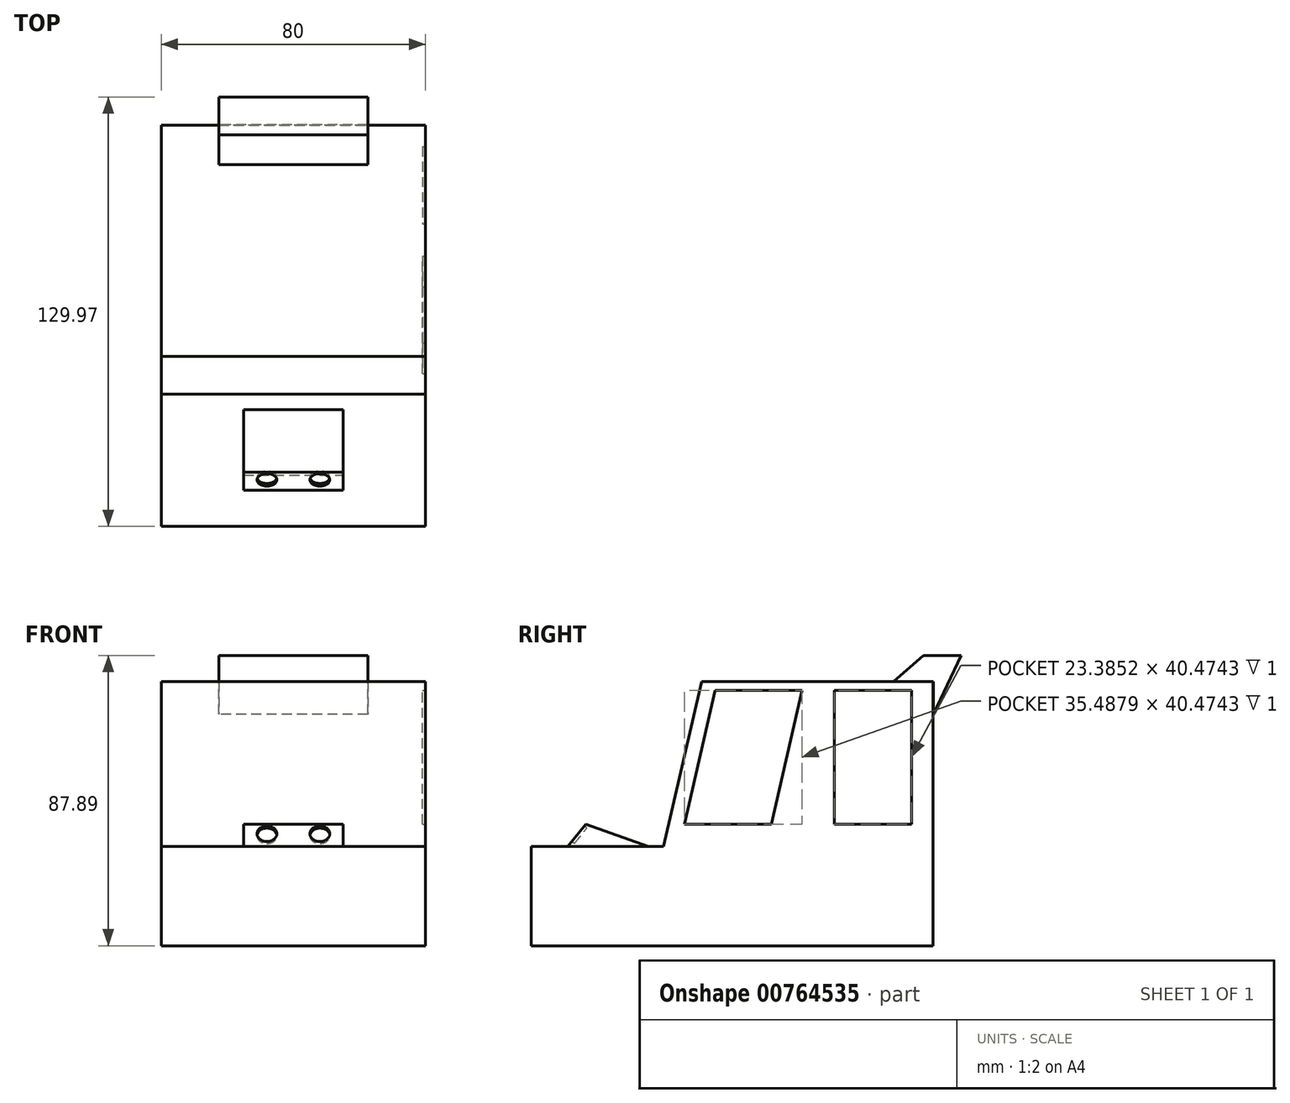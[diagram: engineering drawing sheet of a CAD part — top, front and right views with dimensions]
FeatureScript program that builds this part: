
annotation { "Feature Type Name" : "Feature", "Feature Type Description" : "" }
export const myFeature = defineFeature(function(context is Context, id is Id, definition is map)
    precondition{}
    {
        {
            var Q0;
            Q0=qCreatedBy(makeId("Right.planeOp"),FACE);
            var sketch = newSketch(context, id + "F0", { "sketchPlane" : qUnion([Q0])});
            skLineSegment(sketch, "E0", {"start": v(-34.5, 43.18) * mm, "end": v(35.5, 43.18) * mm});
            skLineSegment(sketch, "E1", {"start": v(35.5, 43.18) * mm, "end": v(35.5, -36.82) * mm});
            skLineSegment(sketch, "E2", {"start": v(35.5, -36.82) * mm, "end": v(-86, -36.82) * mm});
            skLineSegment(sketch, "E3", {"start": v(-86, -36.82) * mm, "end": v(-86, -6.82) * mm});
            skLineSegment(sketch, "E4", {"start": v(-86, -6.82) * mm, "end": v(-46, -6.82) * mm});
            skLineSegment(sketch, "E5", {"start": v(-46, -6.82) * mm, "end": v(-34.5, 43.18) * mm});
            skSolve(sketch);
        }
        {
            var Q0;
            Q0=makeQuery(id+"F0.imprint","IMPRINT",FACE,{"disambiguationData":[TD([[makeQuery(id+"F0.imprint","IMPRINT",EDGE,{"derivedFrom":sQuery(id+"F0.wireOp",EDGE,"E0")}),-1.0]])]});
            extrude(context, id + "F1", {"entities" : qUnion([Q0]), "endBound" : BoundingType.SYMMETRIC, "depth" : 80 * mm, "offsetDistance" : 25 * mm});
        }
        {
            var Q0;
            Q0=qCreatedBy(makeId("Right.planeOp"),FACE);
            var sketch = newSketch(context, id + "F2", { "sketchPlane" : qUnion([Q0])});
            skLineSegment(sketch, "E6", {"start": v(35.58, 33.28) * mm, "end": v(43.97, 51.07) * mm});
            skLineSegment(sketch, "E7", {"start": v(43.97, 51.07) * mm, "end": v(32.58, 51.07) * mm});
            skLineSegment(sketch, "E8", {"start": v(32.58, 51.07) * mm, "end": v(23.38, 43.07) * mm});
            skLineSegment(sketch, "E9", {"start": v(23.38, 43.07) * mm, "end": v(35.58, 43.07) * mm});
            skLineSegment(sketch, "E10", {"start": v(35.58, 43.07) * mm, "end": v(35.58, 33.28) * mm});
            skSolve(sketch);
        }
        {
            var Q0;
            Q0=makeQuery(id+"F2.imprint","IMPRINT",FACE,{"disambiguationData":[TD([[makeQuery(id+"F2.imprint","IMPRINT",EDGE,{"derivedFrom":sQuery(id+"F2.wireOp",EDGE,"E6")}),1.0]])]});
            extrude(context, id + "F3", {"entities" : qUnion([Q0]), "operationType" : NewBodyOperationType.ADD, "endBound" : BoundingType.SYMMETRIC, "depth" : 45 * mm, "offsetDistance" : 25 * mm});
        }
        {
            var Q0;
            Q0=qCreatedBy(makeId("Right.planeOp"),FACE);
            var sketch = newSketch(context, id + "F4", { "sketchPlane" : qUnion([Q0])});
            skLineSegment(sketch, "E11", {"start": v(-50.6, -6.76) * mm, "end": v(-69.54, 0) * mm});
            skLineSegment(sketch, "E12", {"start": v(-69.54, 0) * mm, "end": v(-74.98, -6.83) * mm});
            skLineSegment(sketch, "E13", {"start": v(-74.98, -6.83) * mm, "end": v(-50.6, -6.76) * mm});
            skSolve(sketch);
        }
        {
            var Q0;
            Q0=makeQuery(id+"F4.imprint","IMPRINT",FACE,{"disambiguationData":[TD([[makeQuery(id+"F4.imprint","IMPRINT",EDGE,{"derivedFrom":sQuery(id+"F4.wireOp",EDGE,"E11")}),1.0]])]});
            extrude(context, id + "F5", {"entities" : qUnion([Q0]), "operationType" : NewBodyOperationType.ADD, "endBound" : BoundingType.SYMMETRIC, "depth" : 30 * mm, "offsetDistance" : 25 * mm});
        }
        {
            var Q0;
            Q0=makeQuery(id+"F5.opExtrude","SWEPT_FACE",FACE,{"disambiguationData":[OSD([sQuery(id+"F4.wireOp",EDGE,"E12")])]});
            var sketch = newSketch(context, id + "F6", { "sketchPlane" : qUnion([Q0])});
            skCircle(sketch, "E14", {"center": v(-8, -47.07) * mm, "radius": 3 * mm});
            skCircle(sketch, "E15", {"center": v(8.03, -47.07) * mm, "radius": 3 * mm});
            skSolve(sketch);
        }
        {
            var Q0;
            Q0=makeQuery(id+"F6.imprint","IMPRINT",FACE,{"disambiguationData":[TD([[makeQuery(id+"F6.imprint","IMPRINT",EDGE,{"derivedFrom":sQuery(id+"F6.wireOp",EDGE,"E14")}),1.0]])]});
            var Q1;
            Q1=makeQuery(id+"F6.imprint","IMPRINT",FACE,{"disambiguationData":[TD([[makeQuery(id+"F6.imprint","IMPRINT",EDGE,{"derivedFrom":sQuery(id+"F6.wireOp",EDGE,"E15")}),1.0]])]});
            extrude(context, id + "F7", {"entities" : qUnion([Q0, Q1]), "operationType" : NewBodyOperationType.REMOVE, "oppositeDirection" : true, "depth" : 1 * mm, "offsetDistance" : 25 * mm});
        }
        {
            var Q0;
            Q0=makeQuery(id+"F1.opExtrude","CAP_FACE",FACE,{"disambiguationData":[OSD([sQuery(id+"F0.wireOp",EDGE,"E0"),sQuery(id+"F0.wireOp",EDGE,"E1"),sQuery(id+"F0.wireOp",EDGE,"E2"),sQuery(id+"F0.wireOp",EDGE,"E3"),sQuery(id+"F0.wireOp",EDGE,"E4"),sQuery(id+"F0.wireOp",EDGE,"E5")])],"isStart":false});
            var sketch = newSketch(context, id + "F8", { "sketchPlane" : qUnion([Q0])});
            skLineSegment(sketch, "E16", {"start": v(-30.38, 40.47) * mm, "end": v(-39.69, 0) * mm});
            skLineSegment(sketch, "E17", {"start": v(-39.69, 0) * mm, "end": v(-13.4, 0) * mm});
            skLineSegment(sketch, "E18", {"start": v(-13.4, 0) * mm, "end": v(-4.2, 40.47) * mm});
            skLineSegment(sketch, "E19", {"start": v(-4.2, 40.47) * mm, "end": v(-30.38, 40.47) * mm});
            skLineSegment(sketch, "E20", {"start": v(5.6, 0) * mm, "end": v(5.6, 40.47) * mm});
            skLineSegment(sketch, "E21", {"start": v(5.6, 40.47) * mm, "end": v(28.98, 40.47) * mm});
            skLineSegment(sketch, "E22", {"start": v(28.98, 40.47) * mm, "end": v(28.98, 0) * mm});
            skLineSegment(sketch, "E23", {"start": v(28.98, 0) * mm, "end": v(5.6, 0) * mm});
            skSolve(sketch);
        }
        {
            var Q0;
            Q0=makeQuery(id+"F8.imprint","IMPRINT",FACE,{"disambiguationData":[TD([[makeQuery(id+"F8.imprint","IMPRINT",EDGE,{"derivedFrom":sQuery(id+"F8.wireOp",EDGE,"E16")}),1.0]])]});
            var Q1;
            Q1=makeQuery(id+"F8.imprint","IMPRINT",FACE,{"disambiguationData":[TD([[makeQuery(id+"F8.imprint","IMPRINT",EDGE,{"derivedFrom":sQuery(id+"F8.wireOp",EDGE,"E20")}),-1.0]])]});
            extrude(context, id + "F9", {"entities" : qUnion([Q0, Q1]), "operationType" : NewBodyOperationType.REMOVE, "oppositeDirection" : true, "depth" : 1 * mm, "offsetDistance" : 25 * mm});
        }
    });
